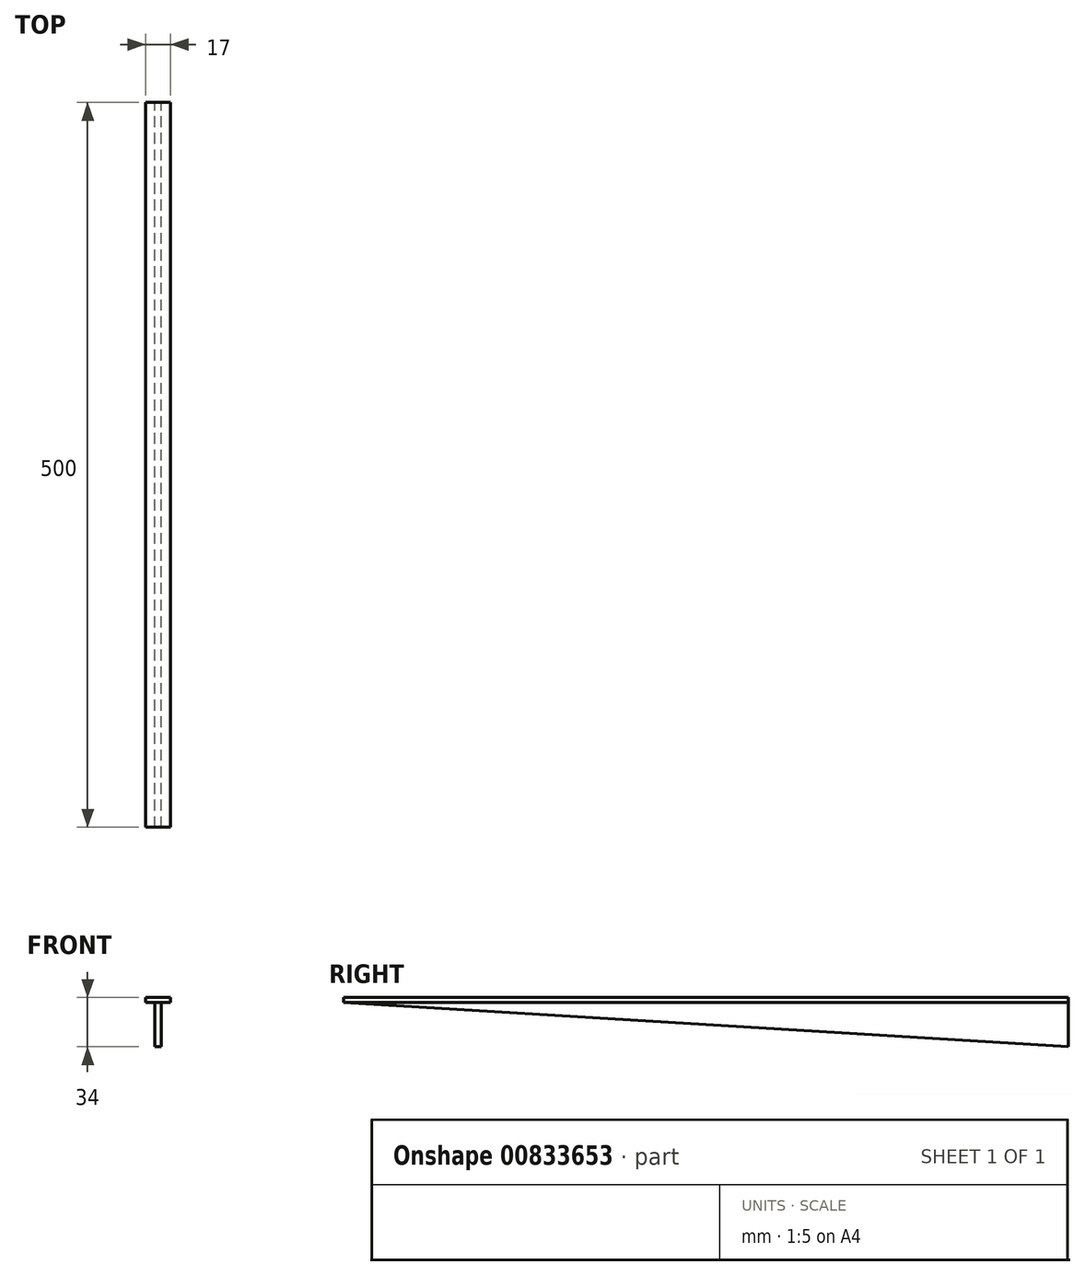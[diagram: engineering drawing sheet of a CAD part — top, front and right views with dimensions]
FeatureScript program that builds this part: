
annotation { "Feature Type Name" : "Feature", "Feature Type Description" : "" }
export const myFeature = defineFeature(function(context is Context, id is Id, definition is map)
    precondition{}
    {
        {
            var Q0;
            Q0=qCreatedBy(makeId("Front.planeOp"),FACE);
            var sketch = newSketch(context, id + "F0", { "sketchPlane" : qUnion([Q0])});
            skLineSegment(sketch, "E0", {"start": v(-8.5, 16.43) * mm, "end": v(0, 16.43) * mm});
            skLineSegment(sketch, "E1", {"start": v(-8.5, 16.43) * mm, "end": v(-8.5, 13.15) * mm});
            skLineSegment(sketch, "E2", {"start": v(-8.5, 13.15) * mm, "end": v(-2.3, 13.15) * mm});
            skLineSegment(sketch, "E3", {"start": v(-2.3, 13.15) * mm, "end": v(-2.3, -17.57) * mm});
            skLineSegment(sketch, "E4", {"start": v(-2.3, -17.57) * mm, "end": v(0, -17.57) * mm});
            skLineSegment(sketch, "E5.MirrorCS", {"start": v(8.5, 16.43) * mm, "end": v(0, 16.43) * mm});
            skLineSegment(sketch, "E6.MirrorCS", {"start": v(8.5, 16.43) * mm, "end": v(8.5, 13.15) * mm});
            skLineSegment(sketch, "E7.MirrorCS", {"start": v(8.5, 13.15) * mm, "end": v(2.3, 13.15) * mm});
            skLineSegment(sketch, "E8.MirrorCS", {"start": v(2.3, 13.15) * mm, "end": v(2.3, -17.57) * mm});
            skLineSegment(sketch, "E9.MirrorCS", {"start": v(2.3, -17.57) * mm, "end": v(0, -17.57) * mm});
            skSolve(sketch);
        }
        {
            var Q0;
            Q0=makeQuery(id+"F0.imprint","IMPRINT",FACE,{"disambiguationData":[TD([[makeQuery(id+"F0.imprint","IMPRINT",EDGE,{"derivedFrom":sQuery(id+"F0.wireOp",EDGE,"E0")}),-1.0]])]});
            extrude(context, id + "F1", {"entities" : qUnion([Q0]), "depth" : 500 * mm, "offsetDistance" : 25 * mm});
        }
        {
            var Q0;
            Q0=makeQuery(id+"F1.opExtrude","SWEPT_FACE",FACE,{"disambiguationData":[OSD([sQuery(id+"F0.wireOp",EDGE,"E8.MirrorCS")])]});
            var sketch = newSketch(context, id + "F2", { "sketchPlane" : qUnion([Q0])});
            skLineSegment(sketch, "E10", {"start": v(-500, 13.15) * mm, "end": v(0, -17.57) * mm});
            skSolve(sketch);
        }
        {
            var Q0;
            Q0=makeQuery(id+"F2.imprint","IMPRINT",FACE,{"disambiguationData":[TD([[makeQuery(id+"F2.imprint","IMPRINT",EDGE,{"derivedFrom":sQuery(id+"F2.wireOp",EDGE,"E10")}),-1.0]])]});
            extrude(context, id + "F3", {"entities" : qUnion([Q0]), "operationType" : NewBodyOperationType.REMOVE, "oppositeDirection" : true, "depth" : 100 * mm, "offsetDistance" : 25 * mm});
        }
    });
